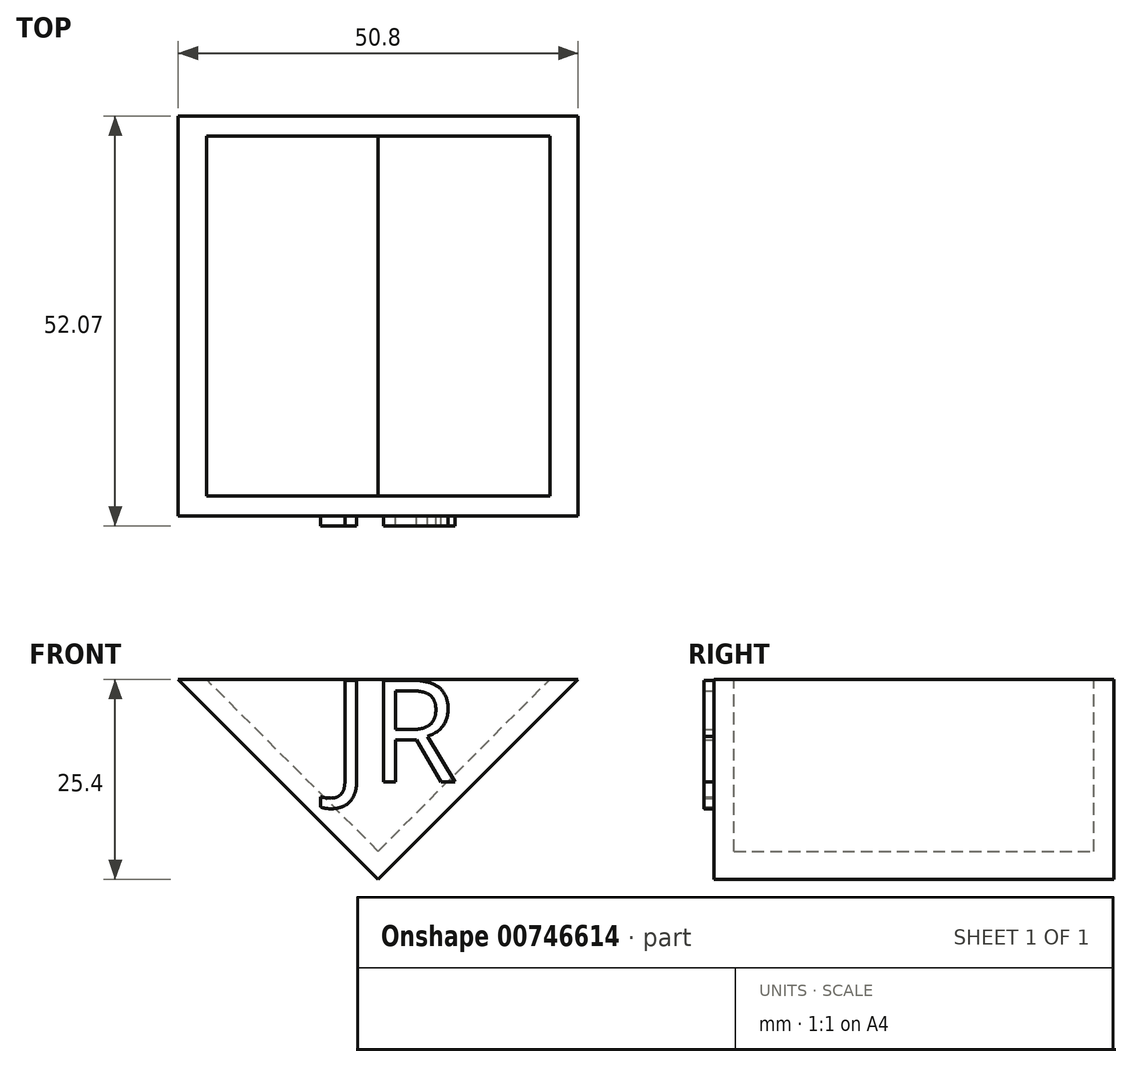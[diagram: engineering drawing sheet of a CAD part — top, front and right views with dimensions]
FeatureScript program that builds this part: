
annotation { "Feature Type Name" : "Feature", "Feature Type Description" : "" }
export const myFeature = defineFeature(function(context is Context, id is Id, definition is map)
    precondition{}
    {
        {
            var Q0;
            Q0=qCreatedBy(makeId("Front.planeOp"),FACE);
            var sketch = newSketch(context, id + "F0", { "sketchPlane" : qUnion([Q0])});
            skLineSegment(sketch, "E0", {"start": v(-25.4, -5.88) * mm, "end": v(25.4, -5.88) * mm});
            skLineSegment(sketch, "E1", {"start": v(0, -31.28) * mm, "end": v(-25.4, -5.88) * mm});
            skLineSegment(sketch, "E2", {"start": v(0, -31.28) * mm, "end": v(25.4, -5.88) * mm});
            skSolve(sketch);
        }
        {
            var Q0;
            Q0 = qSketchRegion(id + "F0", true);
            extrude(context, id + "F1", {"entities" : qUnion([Q0]), "depth" : 50.8 * mm, "offsetDistance" : 25.4 * mm});
        }
        {
            var Q0;
            Q0=makeQuery(id+"F1.opExtrude","SWEPT_FACE",FACE,{"disambiguationData":[OSD([sQuery(id+"F0.wireOp",EDGE,"E0")])]});
            shell(context, id + "F2", {"entities" : qUnion([Q0]), "thickness" : 2.54 * mm});
        }
        {
            var Q0;
            Q0=makeQuery(id+"F1.opExtrude","CAP_FACE",FACE,{"disambiguationData":[OSD([sQuery(id+"F0.wireOp",EDGE,"E0"),sQuery(id+"F0.wireOp",EDGE,"E1"),sQuery(id+"F0.wireOp",EDGE,"E2")])],"isStart":false});
            var sketch = newSketch(context, id + "F3", { "sketchPlane" : qUnion([Q0])});
            skText(sketch, "E3", { "text": "JR", "fontName": "OpenSans-Regular.ttf"});
            const initialGuessF3  = {"E3": [-0.00591, -0.0189, 1, 0, 0.01302]};
            skSetInitialGuess(sketch, initialGuessF3);
            skSolve(sketch);
        }
        {
            var Q0;
            Q0 = qSketchRegion(id + "F3", true);
            extrude(context, id + "F4", {"entities" : qUnion([Q0]), "operationType" : NewBodyOperationType.ADD, "depth" : 1.27 * mm, "offsetDistance" : 25.4 * mm});
        }
    });
